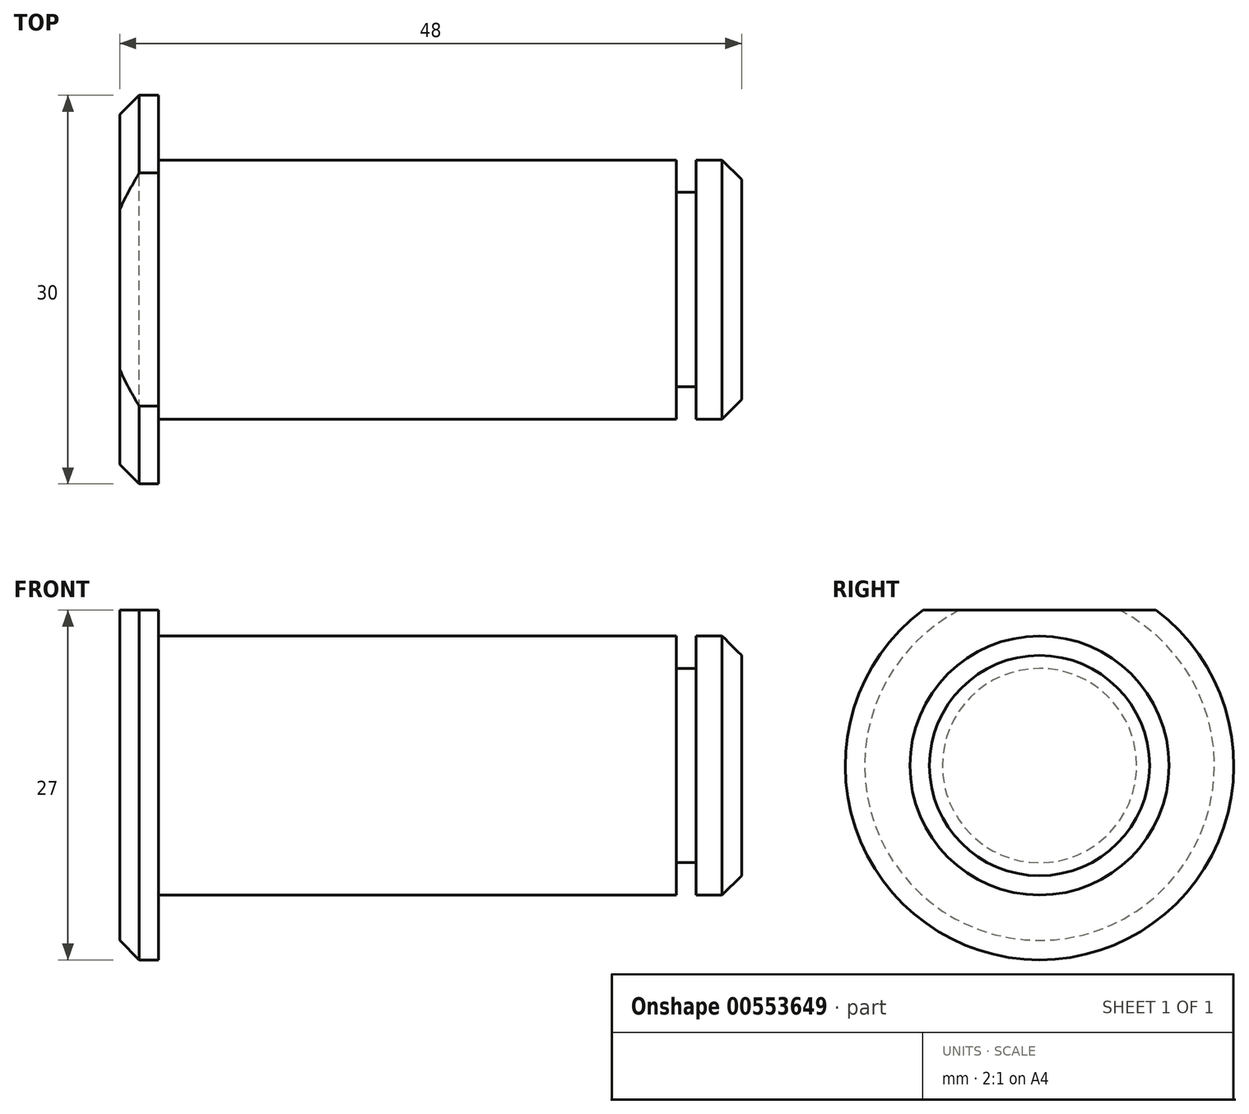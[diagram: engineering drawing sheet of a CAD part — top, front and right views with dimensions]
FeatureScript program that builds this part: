
annotation { "Feature Type Name" : "Feature", "Feature Type Description" : "" }
export const myFeature = defineFeature(function(context is Context, id is Id, definition is map)
    precondition{}
    {
        {
            var Q0;
            Q0=qCreatedBy(makeId("Front.planeOp"),FACE);
            var sketch = newSketch(context, id + "F0", { "sketchPlane" : qUnion([Q0])});
            skLineSegment(sketch, "E0", {"start": v(0, 15) * mm, "end": v(-3, 15) * mm});
            skLineSegment(sketch, "E1", {"start": v(-3, 15) * mm, "end": v(-3, 0) * mm});
            skLineSegment(sketch, "E2", {"start": v(-3, 0) * mm, "end": v(45, 0) * mm});
            skLineSegment(sketch, "E3", {"start": v(45, 0) * mm, "end": v(45, 10) * mm});
            skLineSegment(sketch, "E4", {"start": v(45, 10) * mm, "end": v(41.5, 10) * mm});
            skLineSegment(sketch, "E5", {"start": v(41.5, 10) * mm, "end": v(41.5, 7.5) * mm});
            skLineSegment(sketch, "E6", {"start": v(41.5, 7.5) * mm, "end": v(39.95, 7.5) * mm});
            skLineSegment(sketch, "E7", {"start": v(39.95, 7.5) * mm, "end": v(39.95, 10) * mm});
            skLineSegment(sketch, "E8", {"start": v(39.95, 10) * mm, "end": v(0, 10) * mm});
            skLineSegment(sketch, "E9", {"start": v(0, 10) * mm, "end": v(0, 15) * mm});
            skSolve(sketch);
        }
        {
            var Q0;
            Q0=makeQuery(id+"F0.imprint","IMPRINT",FACE,{"disambiguationData":[TD([[makeQuery(id+"F0.imprint","IMPRINT",EDGE,{"derivedFrom":sQuery(id+"F0.wireOp",EDGE,"E0")}),1.0]])]});
            var Q1;
            Q1=sQuery(id+"F0.wireOp",EDGE,"E2");
            revolve(context, id + "F1", {"entities" : qUnion([Q0]), "axis" : qUnion([Q1]), "revolveType" : RevolveType.FULL});
        }
        {
            var Q0;
            Q0=makeQuery(id+"F1.opRevolve","SWEPT_EDGE",EDGE,{"disambiguationData":[OSD([sQuery(id+"F0.wireOp",EDGE,"E3"),sQuery(id+"F0.wireOp",EDGE,"E4")])]});
            var Q1;
            Q1=makeQuery(id+"F1.opRevolve","SWEPT_EDGE",EDGE,{"disambiguationData":[OSD([sQuery(id+"F0.wireOp",EDGE,"E0"),sQuery(id+"F0.wireOp",EDGE,"E1")])]});
            chamfer(context, id + "F2", {"entities" : qUnion([Q0, Q1]), "width" : 1.5 * mm, "tangentPropagation" : true});
        }
        {
            var Q0;
            Q0=qCreatedBy(makeId("Right.planeOp"),FACE);
            var sketch = newSketch(context, id + "F3", { "sketchPlane" : qUnion([Q0])});
            skLineSegment(sketch, "E10.bottom", {"start": v(15, 15) * mm, "end": v(-15, 15) * mm});
            skLineSegment(sketch, "E10.top", {"start": v(15, 12) * mm, "end": v(-15, 12) * mm});
            skLineSegment(sketch, "E10.left", {"start": v(15, 15) * mm, "end": v(15, 12) * mm});
            skLineSegment(sketch, "E10.right", {"start": v(-15, 15) * mm, "end": v(-15, 12) * mm});
            skLineSegment(sketch, "E11", {"start": v(0, 15) * mm, "end": v(0, 12) * mm, "construction": true});
            skSolve(sketch);
        }
        {
            var Q0;
            Q0 = qSketchRegion(id + "F3", true);
            extrude(context, id + "F4", {"entities" : qUnion([Q0]), "operationType" : NewBodyOperationType.REMOVE, "endBound" : BoundingType.THROUGH_ALL, "oppositeDirection" : true, "depth" : 25 * mm, "offsetDistance" : 25 * mm});
        }
    });
